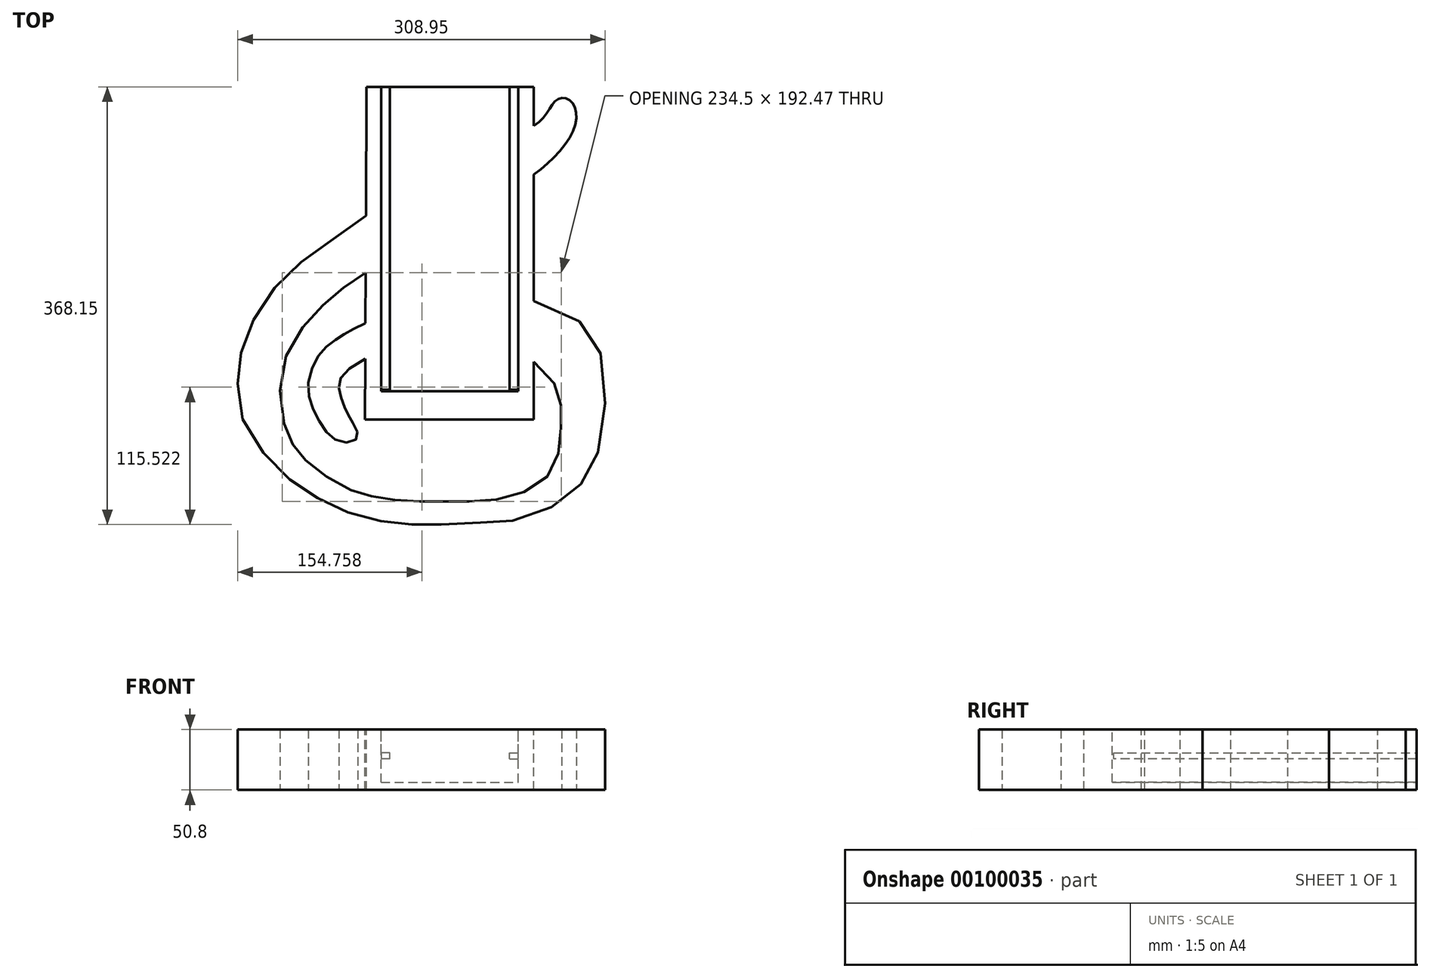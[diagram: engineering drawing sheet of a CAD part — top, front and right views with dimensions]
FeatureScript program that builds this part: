
annotation { "Feature Type Name" : "Feature", "Feature Type Description" : "" }
export const myFeature = defineFeature(function(context is Context, id is Id, definition is map)
    precondition{}
    {
        {
            var Q0;
            Q0=qCreatedBy(makeId("Top.planeOp"),FACE);
            var sketch = newSketch(context, id + "F0", { "sketchPlane" : qUnion([Q0])});
            skFitSpline(sketch, "E0", {"points": [v(125.73, 190) * mm, v(114.17, 190.65) * mm, v(102, 174.1) * mm, v(64.71, 156.03) * mm, v(20.76, 134.4) * mm, v(0, 123.44) * mm, v(-15.22, 114.43) * mm, v(-31.88, 103.02) * mm, v(-46.64, 92.82) * mm, v(-82.08, 67.51) * mm, v(-103.74, 51.5) * mm, v(-126.4, 28.25) * mm, v(-143.16, 0) * mm, v(-151.68, -25.37) * mm, v(-153.8, -47.24) * mm, v(-150.36, -76.29) * mm, v(-132.1, -106.4) * mm, v(-109.1, -129.39) * mm, v(-87.73, -143.48) * mm, v(-65.22, -154.74) * mm, v(-40.7, -162.42) * mm, v(-14.01, -166.06) * mm, v(0, -166.5) * mm, v(26.49, -166.26) * mm, v(60.74, -164.41) * mm, v(82.24, -162.31) * mm, v(120.48, -145.7) * mm, v(139.04, -126.37) * mm, v(152.18, -93.9) * mm, v(152.96, -31.26) * mm, v(138.27, 0) * mm, v(88, 22.87) * mm, v(11.97, 19.56) * mm, v(-20, 12.16) * mm, v(-52.38, 0) * mm, v(-69.41, -9.7) * mm, v(-85.43, -23.8) * mm, v(-94.6, -53.78) * mm, v(-84.49, -80.71) * mm, v(-68.3, -96.77) * mm, v(-53.29, -93.57) * mm, v(-57.16, -81.12) * mm, v(-63.1, -70.1) * mm, v(-68.26, -54.85) * mm, v(-64.61, -39.46) * mm, v(-4.24, -12.49) * mm, v(43.15, -9.6) * mm, v(76.4, -18.11) * mm, v(110.43, -45.18) * mm, v(118.16, -68.38) * mm, v(117.39, -93.9) * mm, v(109.65, -122.5) * mm, v(79.96, -141.66) * mm, v(45.04, -147.1) * mm, v(16.02, -147.16) * mm, v(-11.42, -146.71) * mm, v(-38.5, -143.4) * mm, v(-58.45, -137.65) * mm, v(-89.64, -118.9) * mm, v(-105.12, -102.9) * mm, v(-114.43, -83.74) * mm, v(-115.7, -32.5) * mm, v(-90.78, 9.36) * mm, v(-64.72, 32.61) * mm, v(-36.56, 51.57) * mm, v(-7.13, 71.18) * mm, v(12.52, 82.13) * mm, v(51.54, 104.5) * mm, v(95.8, 128.29) * mm, v(129.86, 169.37) * mm, v(125.73, 190) * mm]});
            skPoint(sketch, "E1", {"position": v(45.04, -165.27) * mm});
            skSolve(sketch);
        }
        {
            var Q0;
            Q0 = qSketchRegion(id + "F0", true);
            extrude(context, id + "F1", {"entities" : qUnion([Q0]), "depth" : 50.8 * mm});
        }
        {
            var Q0;
            Q0=makeQuery(id+"F1.opExtrude","CAP_FACE",FACE,{"disambiguationData":[OSD([sQuery(id+"F0.wireOp",EDGE,"E0")])],"isStart":false});
            var sketch = newSketch(context, id + "F2", { "sketchPlane" : qUnion([Q0])});
            skLineSegment(sketch, "E2.top", {"start": v(94.63, 636.97) * mm, "end": v(-46.07, 636.97) * mm});
            skPoint(sketch, "E3", {"position": v(-46.8, -78.4) * mm});
            skLineSegment(sketch, "E4", {"start": v(95.17, -78.4) * mm, "end": v(-46.8, -78.4) * mm});
            skPoint(sketch, "E5", {"position": v(95.17, 201.6) * mm});
            skPoint(sketch, "E6", {"position": v(-45.53, 201.6) * mm});
            skLineSegment(sketch, "E7", {"start": v(-45.53, 201.6) * mm, "end": v(95.17, 201.6) * mm});
            skLineSegment(sketch, "E8", {"start": v(95.17, 201.6) * mm, "end": v(95.17, -78.4) * mm});
            skLineSegment(sketch, "E9", {"start": v(-45.53, 201.6) * mm, "end": v(-46.8, -78.4) * mm});
            skSolve(sketch);
        }
        {
            var Q0;
            {var subQ0=sQuery(id+"F2.wireOp",EDGE,"E7");Q0=makeQuery(id+"F2.imprint","IMPRINT",FACE,{"disambiguationData":[TD([[makeQuery(id+"F2.imprint","IMPRINT",EDGE,{"derivedFrom":subQ0}),-1.0]])]});}
            var Q1;
            {var subQ0=sQuery(id+"F2.wireOp",EDGE,"E2.left");var subQ1=makeQuery(id+"F1.opExtrude","CAP_EDGE",EDGE,{"disambiguationData":[OSD([sQuery(id+"F0.wireOp",EDGE,"E0")])],"isStart":false});var subQ2=makeQuery(id+"F2.imprint","INTERSECT",VERTEX,{"disambiguationData":[OD(1.0)],"derivedFrom":[subQ1,subQ0]});Q1=makeQuery(id+"F2.imprint","IMPRINT",FACE,{"disambiguationData":[TD([[makeQuery(id+"F2.imprint","IMPRINT",EDGE,{"disambiguationData":[TD([[subQ2,-1.0]])],"derivedFrom":subQ0}),1.0]])]});}
            var Q2;
            {var subQ6=sQuery(id+"F2.wireOp",EDGE,"E2.bottom");Q2=makeQuery(id+"F2.imprint","IMPRINT",FACE,{"disambiguationData":[TD([[makeQuery(id+"F2.imprint","IMPRINT",EDGE,{"derivedFrom":subQ6}),-1.0]])]});}
            var Q3;
            {var subQ1=sQuery(id+"F2.wireOp",EDGE,"E2.bottom");Q3=makeQuery(id+"F2.imprint","IMPRINT",FACE,{"disambiguationData":[TD([[makeQuery(id+"F2.imprint","IMPRINT",EDGE,{"derivedFrom":subQ1}),1.0]])]});}
            var Q4;
            {var subQ0=sQuery(id+"F2.wireOp",EDGE,"E4");Q4=makeQuery(id+"F2.imprint","IMPRINT",FACE,{"disambiguationData":[TD([[makeQuery(id+"F2.imprint","IMPRINT",EDGE,{"derivedFrom":subQ0}),-1.0]])]});}
            var Q5;
            {var subQ0=sQuery(id+"F2.wireOp",EDGE,"pUi5V6yo-zhLt-0BLL-0ix0-JjyO4qd6jAw0");var subQ1=makeQuery(id+"F1.opExtrude","CAP_EDGE",EDGE,{"disambiguationData":[OSD([sQuery(id+"F0.wireOp",EDGE,"E0")])],"isStart":false});var subQ2=makeQuery(id+"F2.imprint","INTERSECT",VERTEX,{"disambiguationData":[OD(1.0)],"derivedFrom":[subQ1,subQ0]});Q5=makeQuery(id+"F2.imprint","IMPRINT",FACE,{"disambiguationData":[TD([[makeQuery(id+"F2.imprint","IMPRINT",EDGE,{"disambiguationData":[TD([[subQ2,-1.0]])],"derivedFrom":subQ0}),1.0]])]});}
            var Q6;
            {var subQ1=makeQuery(id+"F1.opExtrude","CAP_EDGE",EDGE,{"disambiguationData":[OSD([sQuery(id+"F0.wireOp",EDGE,"E0")])],"isStart":false});var subQ4=sQuery(id+"F2.wireOp",EDGE,"pUi5V6yo-zhLt-0BLL-0ix0-JjyO4qd6jAw0");var subQ8=makeQuery(id+"F2.imprint","INTERSECT",VERTEX,{"disambiguationData":[OD(0.0)],"derivedFrom":[subQ1,subQ4]});Q6=makeQuery(id+"F2.imprint","IMPRINT",FACE,{"disambiguationData":[TD([[makeQuery(id+"F2.imprint","IMPRINT",EDGE,{"disambiguationData":[TD([[subQ8,-1.0]])],"derivedFrom":subQ4}),1.0]])]});}
            var Q7;
            {var subQ0=sQuery(id+"F2.wireOp",EDGE,"E2.left");var subQ1=makeQuery(id+"F1.opExtrude","CAP_EDGE",EDGE,{"disambiguationData":[OSD([sQuery(id+"F0.wireOp",EDGE,"E0")])],"isStart":false});var subQ2=makeQuery(id+"F2.imprint","INTERSECT",VERTEX,{"disambiguationData":[OD(0.0)],"derivedFrom":[subQ1,subQ0]});Q7=makeQuery(id+"F2.imprint","IMPRINT",FACE,{"disambiguationData":[TD([[makeQuery(id+"F2.imprint","IMPRINT",EDGE,{"disambiguationData":[TD([[subQ2,-1.0]])],"derivedFrom":subQ0}),1.0]])]});}
            var Q8;
            {var subQ0=sQuery(id+"F2.wireOp",EDGE,"E8");var subQ1=makeQuery(id+"F1.opExtrude","CAP_EDGE",EDGE,{"disambiguationData":[OSD([sQuery(id+"F0.wireOp",EDGE,"E0")])],"isStart":false});var subQ2=makeQuery(id+"F2.imprint","INTERSECT",VERTEX,{"disambiguationData":[OD(1.0)],"derivedFrom":[subQ1,subQ0]});Q8=makeQuery(id+"F2.imprint","IMPRINT",FACE,{"disambiguationData":[TD([[makeQuery(id+"F2.imprint","IMPRINT",EDGE,{"disambiguationData":[TD([[subQ2,-1.0]])],"derivedFrom":subQ0}),-1.0]])]});}
            extrude(context, id + "F3", {"entities" : qUnion([Q0, Q1, Q2, Q3, Q4, Q5, Q6, Q7, Q8]), "operationType" : NewBodyOperationType.ADD, "oppositeDirection" : true, "depth" : 50.8 * mm});
        }
        {
            var Q0;
            {var subQ0=sQuery(id+"F2.wireOp",EDGE,"E2.left");var subQ1=sQuery(id+"F0.wireOp",EDGE,"E0");Q0=makeQuery(id+"F3.boolean.opBoolean","MERGE",FACE,{"derivedFrom":[makeQuery(id+"F1.opExtrude","CAP_FACE",FACE,{"disambiguationData":[OSD([subQ1])],"isStart":false}),makeQuery(id+"F3.opExtrude","CAP_FACE",FACE,{"disambiguationData":[OSD([subQ1,subQ0,sQuery(id+"F2.wireOp",EDGE,"pUi5V6yo-zhLt-0BLL-0ix0-JjyO4qd6jAw0"),sQuery(id+"F2.wireOp",EDGE,"CnXaO7K9-1izv-dOOB-x8eX-SiNJ0DRP5LU1"),sQuery(id+"F2.wireOp",EDGE,"E4")])],"isStart":true}),makeQuery(id+"F3.opExtrude","CAP_FACE",FACE,{"disambiguationData":[OSD([subQ1,subQ0,sQuery(id+"F2.wireOp",EDGE,"E2.right"),sQuery(id+"F2.wireOp",EDGE,"E7")])],"isStart":true})]});}
            var sketch = newSketch(context, id + "F4", { "sketchPlane" : qUnion([Q0])});
            skLineSegment(sketch, "E10", {"start": v(81.93, 201.6) * mm, "end": v(-33.37, 201.6) * mm});
            skLineSegment(sketch, "E11", {"start": v(-33.37, 201.6) * mm, "end": v(-33.37, -54.4) * mm});
            skLineSegment(sketch, "E12", {"start": v(-33.37, -54.4) * mm, "end": v(81.93, -54.41) * mm});
            skLineSegment(sketch, "E13", {"start": v(81.93, -54.41) * mm, "end": v(81.93, 201.6) * mm});
            skSolve(sketch);
        }
        {
            var Q0;
            Q0=makeQuery(id+"F4.imprint","IMPRINT",FACE,{"disambiguationData":[TD([[makeQuery(id+"F4.imprint","IMPRINT",EDGE,{"derivedFrom":sQuery(id+"F4.wireOp",EDGE,"E10")}),-1.0]])]});
            extrude(context, id + "F5", {"entities" : qUnion([Q0]), "operationType" : NewBodyOperationType.REMOVE, "oppositeDirection" : true, "depth" : 44.45 * mm});
        }
        {
            var Q0;
            Q0=makeQuery(id+"F5.boolean.opBoolean","COPY",FACE,{"derivedFrom":makeQuery(id+"F5.opExtrude","SWEPT_FACE",FACE,{"disambiguationData":[OSD([sQuery(id+"F4.wireOp",EDGE,"E11")])]})});
            var sketch = newSketch(context, id + "F6", { "sketchPlane" : qUnion([Q0])});
            skLineSegment(sketch, "E14", {"start": v(201.6, 50.8) * mm, "end": v(201.6, 31.08) * mm, "construction": true});
            skLineSegment(sketch, "E15", {"start": v(201.6, 31.08) * mm, "end": v(201.6, 26.07) * mm});
            skLineSegment(sketch, "E16", {"start": v(201.6, 31.08) * mm, "end": v(-53.1, 31.08) * mm});
            skLineSegment(sketch, "E17", {"start": v(-53.1, 31.07) * mm, "end": v(-53.1, 26.07) * mm});
            skLineSegment(sketch, "E18", {"start": v(-53.1, 26.07) * mm, "end": v(201.6, 26.07) * mm});
            skSolve(sketch);
        }
        {
            var Q0;
            Q0=makeQuery(id+"F5.boolean.opBoolean","COPY",FACE,{"derivedFrom":makeQuery(id+"F5.opExtrude","SWEPT_FACE",FACE,{"disambiguationData":[OSD([sQuery(id+"F4.wireOp",EDGE,"E13")])]})});
            var sketch = newSketch(context, id + "F7", { "sketchPlane" : qUnion([Q0])});
            skLineSegment(sketch, "E19", {"start": v(-201.59, 50.8) * mm, "end": v(-201.59, 31.07) * mm, "construction": true});
            skLineSegment(sketch, "E20", {"start": v(-201.59, 26.08) * mm, "end": v(-201.59, 6.35) * mm, "construction": true});
            skLineSegment(sketch, "E21", {"start": v(-201.59, 26.08) * mm, "end": v(-201.59, 31.07) * mm});
            skLineSegment(sketch, "E22", {"start": v(-201.59, 26.07) * mm, "end": v(53.1, 26.07) * mm});
            skLineSegment(sketch, "E23", {"start": v(53.1, 26.08) * mm, "end": v(53.1, 31.08) * mm});
            skLineSegment(sketch, "E24", {"start": v(53.1, 31.08) * mm, "end": v(-201.59, 31.07) * mm});
            skSolve(sketch);
        }
        {
            var Q0;
            Q0=makeQuery(id+"F6.imprint","IMPRINT",FACE,{"disambiguationData":[TD([[makeQuery(id+"F6.imprint","IMPRINT",EDGE,{"derivedFrom":sQuery(id+"F6.wireOp",EDGE,"cu86BMoW-Znzf-g9nx-fHRZ-VvTlNmFD3Y11")}),1.0]])]});
            var Q1;
            Q1=makeQuery(id+"F6.imprint","IMPRINT",FACE,{"disambiguationData":[TD([[makeQuery(id+"F6.imprint","IMPRINT",EDGE,{"derivedFrom":sQuery(id+"F6.wireOp",EDGE,"E15")}),1.0]])]});
            extrude(context, id + "F8", {"entities" : qUnion([Q0, Q1]), "operationType" : NewBodyOperationType.ADD, "depth" : 7.35 * mm});
        }
        {
            var Q0;
            Q0=makeQuery(id+"F7.imprint","IMPRINT",FACE,{"disambiguationData":[TD([[makeQuery(id+"F7.imprint","IMPRINT",EDGE,{"derivedFrom":sQuery(id+"F7.wireOp",EDGE,"hKzRBjoP-kNSg-81Z1-94er-dh69Wtns58Ht")}),-1.0]])]});
            var Q1;
            Q1=makeQuery(id+"F7.imprint","IMPRINT",FACE,{"disambiguationData":[TD([[makeQuery(id+"F7.imprint","IMPRINT",EDGE,{"derivedFrom":sQuery(id+"F7.wireOp",EDGE,"E21")}),-1.0]])]});
            extrude(context, id + "F9", {"entities" : qUnion([Q0, Q1]), "operationType" : NewBodyOperationType.ADD, "depth" : 7.35 * mm});
        }
    });
